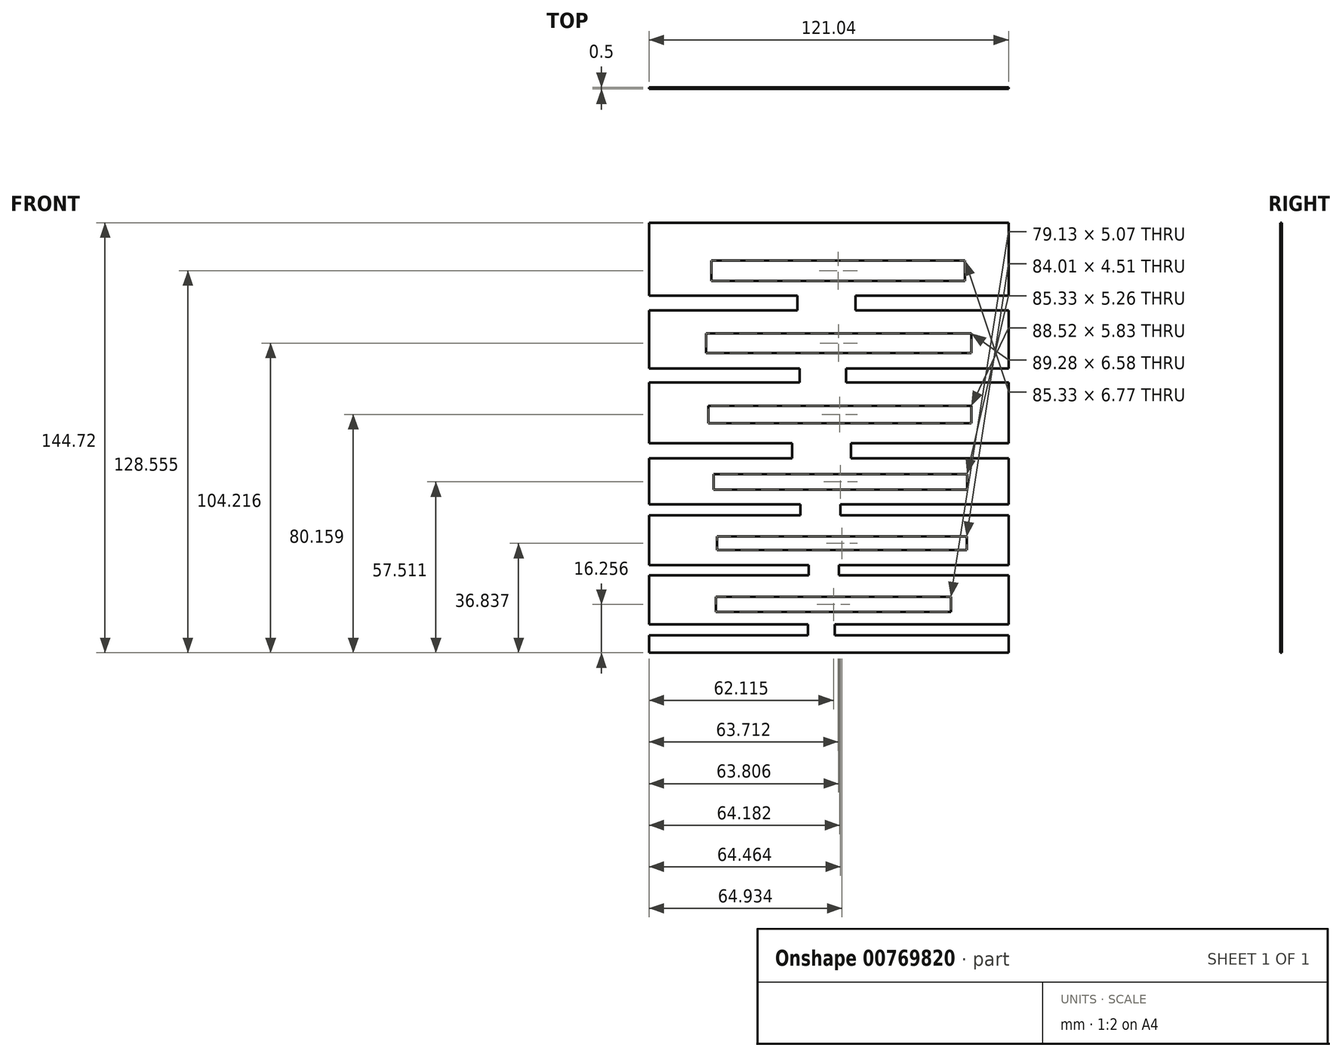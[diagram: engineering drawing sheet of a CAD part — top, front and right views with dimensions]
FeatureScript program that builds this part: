
annotation { "Feature Type Name" : "Feature", "Feature Type Description" : "" }
export const myFeature = defineFeature(function(context is Context, id is Id, definition is map)
    precondition{}
    {
        {
            var Q0;
            Q0=qCreatedBy(makeId("Front.planeOp"),FACE);
            var sketch = newSketch(context, id + "F0", { "sketchPlane" : qUnion([Q0])});
            skLineSegment(sketch, "E0.bottom", {"start": v(-58.36, 71.9) * mm, "end": v(62.68, 71.9) * mm});
            skLineSegment(sketch, "E0.top", {"start": v(-58.36, -72.82) * mm, "end": v(62.68, -72.82) * mm});
            skLineSegment(sketch, "E0.left", {"start": v(-58.36, 71.9) * mm, "end": v(-58.36, 47.37) * mm});
            skLineSegment(sketch, "E0.right", {"start": v(62.68, 71.9) * mm, "end": v(62.68, 47.37) * mm});
            skLineSegment(sketch, "E1.bottom", {"start": v(-58.36, -63.24) * mm, "end": v(-4.8, -63.24) * mm});
            skLineSegment(sketch, "E1.top", {"start": v(-58.36, -67) * mm, "end": v(-4.8, -67) * mm});
            skLineSegment(sketch, "E2", {"start": v(-4.8, -63.24) * mm, "end": v(-4.8, -67) * mm});
            skLineSegment(sketch, "E3", {"start": v(4.22, -63.24) * mm, "end": v(4.22, -67) * mm});
            skLineSegment(sketch, "E4.trimOffspring", {"start": v(4.22, -67) * mm, "end": v(62.68, -67) * mm});
            skLineSegment(sketch, "E5.trimOffspring", {"start": v(4.22, -63.24) * mm, "end": v(62.68, -63.24) * mm});
            skLineSegment(sketch, "E6.trimOffspring", {"start": v(-58.36, -67) * mm, "end": v(-58.36, -72.82) * mm});
            skLineSegment(sketch, "E7.trimOffspring", {"start": v(62.68, -67) * mm, "end": v(62.68, -72.82) * mm});
            skLineSegment(sketch, "E8.bottom", {"start": v(-35.8, -54.03) * mm, "end": v(43.32, -54.03) * mm});
            skLineSegment(sketch, "E8.top", {"start": v(-35.8, -59.1) * mm, "end": v(43.32, -59.1) * mm});
            skLineSegment(sketch, "E8.left", {"start": v(-35.8, -54.03) * mm, "end": v(-35.8, -59.1) * mm});
            skLineSegment(sketch, "E8.right", {"start": v(43.32, -54.03) * mm, "end": v(43.32, -59.1) * mm});
            skLineSegment(sketch, "E9.bottom", {"start": v(-58.36, -46.7) * mm, "end": v(-4.6, -46.7) * mm});
            skLineSegment(sketch, "E9.top", {"start": v(-58.36, -43.31) * mm, "end": v(-4.6, -43.31) * mm});
            skLineSegment(sketch, "E10", {"start": v(-4.6, -43.31) * mm, "end": v(-4.6, -46.7) * mm});
            skLineSegment(sketch, "E11", {"start": v(5.54, -43.31) * mm, "end": v(5.54, -46.7) * mm});
            skLineSegment(sketch, "E12.trimOffspring", {"start": v(5.54, -46.7) * mm, "end": v(62.68, -46.7) * mm});
            skLineSegment(sketch, "E13.trimOffspring", {"start": v(5.54, -43.31) * mm, "end": v(62.68, -43.31) * mm});
            skLineSegment(sketch, "E14.trimOffspring", {"start": v(-58.36, -46.7) * mm, "end": v(-58.36, -63.24) * mm});
            skLineSegment(sketch, "E15.trimOffspring", {"start": v(62.68, -46.7) * mm, "end": v(62.68, -63.24) * mm});
            skLineSegment(sketch, "E16.bottom", {"start": v(-35.43, -33.73) * mm, "end": v(48.58, -33.73) * mm});
            skLineSegment(sketch, "E16.top", {"start": v(-35.43, -38.24) * mm, "end": v(48.58, -38.24) * mm});
            skLineSegment(sketch, "E16.left", {"start": v(-35.43, -33.73) * mm, "end": v(-35.43, -38.24) * mm});
            skLineSegment(sketch, "E16.right", {"start": v(48.58, -33.73) * mm, "end": v(48.58, -38.24) * mm});
            skLineSegment(sketch, "E17.bottom", {"start": v(-58.36, -26.59) * mm, "end": v(-7.43, -26.59) * mm});
            skLineSegment(sketch, "E17.top", {"start": v(-58.36, -22.83) * mm, "end": v(-7.43, -22.83) * mm});
            skLineSegment(sketch, "E18", {"start": v(-7.43, -22.83) * mm, "end": v(-7.43, -26.59) * mm});
            skLineSegment(sketch, "E19", {"start": v(6.1, -22.83) * mm, "end": v(6.1, -26.59) * mm});
            skLineSegment(sketch, "E20.trimOffspring", {"start": v(6.1, -26.59) * mm, "end": v(62.68, -26.59) * mm});
            skLineSegment(sketch, "E21.trimOffspring", {"start": v(6.1, -22.83) * mm, "end": v(62.68, -22.83) * mm});
            skLineSegment(sketch, "E22.trimOffspring", {"start": v(-58.36, -26.59) * mm, "end": v(-58.36, -43.31) * mm});
            skLineSegment(sketch, "E23.trimOffspring", {"start": v(62.68, -26.59) * mm, "end": v(62.68, -43.31) * mm});
            skLineSegment(sketch, "E24.bottom", {"start": v(-36.56, -12.68) * mm, "end": v(48.77, -12.68) * mm});
            skLineSegment(sketch, "E24.top", {"start": v(-36.56, -17.94) * mm, "end": v(48.77, -17.94) * mm});
            skLineSegment(sketch, "E24.left", {"start": v(-36.56, -12.68) * mm, "end": v(-36.56, -17.94) * mm});
            skLineSegment(sketch, "E24.right", {"start": v(48.77, -12.68) * mm, "end": v(48.77, -17.94) * mm});
            skLineSegment(sketch, "E25.bottom", {"start": v(-58.36, -2.34) * mm, "end": v(-10.25, -2.34) * mm});
            skLineSegment(sketch, "E25.top", {"start": v(-58.36, -7.42) * mm, "end": v(-10.25, -7.42) * mm});
            skLineSegment(sketch, "E26", {"start": v(-10.25, -2.34) * mm, "end": v(-10.25, -7.42) * mm});
            skLineSegment(sketch, "E27", {"start": v(9.68, -2.34) * mm, "end": v(9.68, -7.42) * mm});
            skLineSegment(sketch, "E28.trimOffspring", {"start": v(9.68, -7.42) * mm, "end": v(62.68, -7.42) * mm});
            skLineSegment(sketch, "E29.trimOffspring", {"start": v(9.68, -2.34) * mm, "end": v(62.68, -2.34) * mm});
            skLineSegment(sketch, "E30.trimOffspring", {"start": v(-58.36, -7.42) * mm, "end": v(-58.36, -22.83) * mm});
            skLineSegment(sketch, "E31.trimOffspring", {"start": v(62.68, -7.42) * mm, "end": v(62.68, -22.83) * mm});
            skLineSegment(sketch, "E32.bottom", {"start": v(-38.44, 10.25) * mm, "end": v(50.08, 10.25) * mm});
            skLineSegment(sketch, "E32.top", {"start": v(-38.44, 4.43) * mm, "end": v(50.08, 4.43) * mm});
            skLineSegment(sketch, "E32.left", {"start": v(-38.44, 10.25) * mm, "end": v(-38.44, 4.43) * mm});
            skLineSegment(sketch, "E32.right", {"start": v(50.08, 10.25) * mm, "end": v(50.08, 4.43) * mm});
            skLineSegment(sketch, "E33.bottom", {"start": v(-58.36, 22.84) * mm, "end": v(-7.62, 22.84) * mm});
            skLineSegment(sketch, "E33.top", {"start": v(-58.36, 18.15) * mm, "end": v(-7.62, 18.15) * mm});
            skLineSegment(sketch, "E34", {"start": v(-7.62, 22.84) * mm, "end": v(-7.62, 18.15) * mm});
            skLineSegment(sketch, "E35", {"start": v(7.98, 22.84) * mm, "end": v(7.98, 18.15) * mm});
            skLineSegment(sketch, "E36.trimOffspring", {"start": v(7.98, 18.15) * mm, "end": v(62.68, 18.15) * mm});
            skLineSegment(sketch, "E37.trimOffspring", {"start": v(7.98, 22.84) * mm, "end": v(62.68, 22.84) * mm});
            skLineSegment(sketch, "E38.trimOffspring", {"start": v(-58.36, 18.15) * mm, "end": v(-58.36, -2.34) * mm});
            skLineSegment(sketch, "E39.trimOffspring", {"start": v(62.68, 18.15) * mm, "end": v(62.68, -2.34) * mm});
            skLineSegment(sketch, "E40.bottom", {"start": v(-39.2, 34.68) * mm, "end": v(50.08, 34.68) * mm});
            skLineSegment(sketch, "E40.top", {"start": v(-39.2, 28.1) * mm, "end": v(50.08, 28.1) * mm});
            skLineSegment(sketch, "E40.left", {"start": v(-39.2, 34.68) * mm, "end": v(-39.2, 28.1) * mm});
            skLineSegment(sketch, "E40.right", {"start": v(50.08, 34.68) * mm, "end": v(50.08, 28.1) * mm});
            skLineSegment(sketch, "E41.bottom", {"start": v(-58.36, 47.37) * mm, "end": v(-8.37, 47.37) * mm});
            skLineSegment(sketch, "E41.top", {"start": v(-58.36, 42.4) * mm, "end": v(-8.37, 42.4) * mm});
            skLineSegment(sketch, "E42", {"start": v(-8.37, 47.37) * mm, "end": v(-8.37, 42.4) * mm});
            skLineSegment(sketch, "E43", {"start": v(11.18, 47.37) * mm, "end": v(11.18, 42.4) * mm});
            skLineSegment(sketch, "E44.trimOffspring", {"start": v(11.18, 42.4) * mm, "end": v(62.68, 42.4) * mm});
            skLineSegment(sketch, "E45.trimOffspring", {"start": v(11.18, 47.37) * mm, "end": v(62.68, 47.37) * mm});
            skLineSegment(sketch, "E46.trimOffspring", {"start": v(-58.36, 42.4) * mm, "end": v(-58.36, 22.84) * mm});
            skLineSegment(sketch, "E47.trimOffspring", {"start": v(62.68, 42.4) * mm, "end": v(62.68, 22.84) * mm});
            skLineSegment(sketch, "E48.bottom", {"start": v(-37.31, 59.12) * mm, "end": v(48.02, 59.12) * mm});
            skLineSegment(sketch, "E48.top", {"start": v(-37.31, 52.35) * mm, "end": v(48.02, 52.35) * mm});
            skLineSegment(sketch, "E48.left", {"start": v(-37.31, 59.12) * mm, "end": v(-37.31, 52.35) * mm});
            skLineSegment(sketch, "E48.right", {"start": v(48.02, 59.12) * mm, "end": v(48.02, 52.35) * mm});
            skSolve(sketch);
        }
        {
            var Q0;
            Q0=qSketchRegion(id+"F0",true);
            extrude(context, id + "F1", {"entities" : qUnion([Q0]), "depth" : .5 * mm, "offsetDistance" : 25 * mm});
        }
    });
